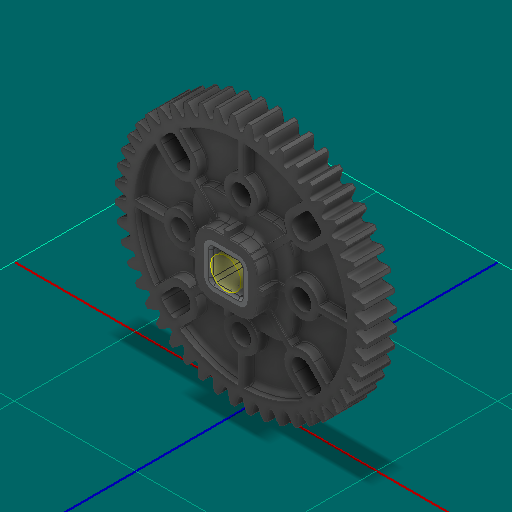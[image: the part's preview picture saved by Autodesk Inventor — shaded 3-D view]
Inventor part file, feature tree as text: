
AUTODESK INVENTOR PART (.ipt)
format: ipt  version: 2025 (Build 290162000, 162)  size: 3,909,632 bytes
history: native  units: in
note: dims shown in document units (in); Inventor stores cm internally (conversion verified against a paired STEP export)
features: other x6, sketch x3
ambient origin geometry x8: Origin, YZ Plane, XZ Plane, XY Plane, X Axis, Y Axis, Z Axis, Center Point
bodies: Solid1 (feature_tree), Solid2 (feature_tree)
feature tree (9):
  other  "Half Cut HS 48T Gear, No Insert.ipt"
  other  "Solid1::Half Cut HS 48T Gear, No Insert.ipt"
  other  "Solid2::Half Cut HS 48T Gear, No Insert.ipt"
  other  "TaggingFeature1"
  sketch  "Sketch1"  dims[d0=0.3937in]
  sketch  "Sketch2"
  sketch  "Sketch3"
  other  "Srf1"
  other  "Srf1::Derived"
